# Revit family: 0052419 Sylvania Lighting RANA LED RECESSED
name_source: partatom
category: Lighting Fixtures
revit_build: Autodesk Revit 2016 (Build: 20150220_1215(x64)
units: mm (PartAtom-declared; Revit-internal decimal feet)

## family parameters
Cut with Voids When Loaded = No
Host = Face
Light Source = Yes
OmniClass Number = 23.80.70.00
OmniClass Title = Lighting
Part Type = Normal
Room Calculation Point = No
Round Connector Dimension = Use Diameter
Shared = No

## types (2) — shared parameters
1200_SYL = No
1Ref_SYL = No
2Ref_SYL = No
600x600_SYL = Yes
625x625_SYL = No
Apparent Load = 44 VA
Assembly Code = D5020200
AssetType = Fixed
ClassificationName = Uniclass2015
ClassificationValue = EF_70_80
Color Filter = 16777215
Default Elevation = 1219 mm
Description = Ceiling Recessed LED Linear luminaire (lay-in), with Louvre + Prismatic Optic, Direct Light Distribution, Luminaire Dimensions: 595x595x60mm, Sylvania White body colour, IP20, IK07, Light Engine Dimensions: 570x285mm, Constant Current, Low LED flicker (+/-5%), Emergency 3 hours, Neutral White (4000K) LED Colour Temperature, 4500lm, 44W, 102lm/W efficacy, CRI>80, 3 SDCM (3-step MacAdam ellipse) LED Colour Consistency, UGR<19, Luminance at 65° < 3000 cd/m2, Lumen Maintenance: L90B10 at 50,000 hours, Glow Wire Test 850°C, Quick and easy electrical connection with direct access to push-connectors on top, 2 x metallic safety cables (1.5m) included, the luminaire can be covered with building insulation of Glass Wool type.
Dimming Lamp Color Temperature Shift = <None>
DocumentationLiterature = http://www.sylvania-lighting.com
ElectricShockClassification = Class I
Emit Shape Visible in Rendering = No
Emit from Rectangle Length = 542 mm  [stored 1.77822 ft]
Emit from Rectangle Width = 282 mm
IfcExportAs = IfcLightFixtureType
IfcExportType = IfcLightFixtureType
ImpactProtectionIndex = IK07
IngressProtection = IP20
Inset_SYL = 20 mm  [stored 0.0656168 ft]
Keynote = 16500
Lamp = LED
LampColourRenderingIndex = 80
LampColourTemperature = 4000 K
LampMacAdamStep = 3
LampsType = LED
Length_SYL = 595 mm  [stored 1.9521 ft]
LouverNumber_SYL = 14
Manufacturer = Feilo Sylvania
ManufacturerName = Feilo Sylvania
Material = steel housing, polycarbonate diffuser
Material_1_SYL = Body-Sylvania-Rana-White
Material_2_SYL = <By Category>
Material_3_SYL = <By Category>
Material_4_SYL = <By Category>
Model = RANA LED R 600 HO 4K LOUV+PRI EM W GEN2
ModelNumber = 0052419
ModelReference = RANA LED R 600 HO 4K LOUV+PRI EM W GEN2
Name = RANA LED R 600 HO 4K LOUV+PRI EM W GEN2
NominalDepth = 595 mm  [stored 1.9521 ft]
NominalHeight = 60 mm
NominalLength = 595 mm  [stored 1.9521 ft]
PowerConsumption = 44 W
PowerFactor = 0.95
ReflectorInset_SYL = 30 mm  [stored 0.0984252 ft]
ReflectorLength_SYL = 550 mm
ReflectorNumber_SYL = 3
SlopeBottomWidth_SYL = 593 mm  [stored 1.94554 ft]
SlopeHeight_SYL = 17 mm
SlopeTopWidth_SYL = 410 mm  [stored 1.34514 ft]
Tilt Angle = -90.00°
TopWidth_SYL = 295 mm  [stored 0.967848 ft]
Type Image = <None>
TypeName = RANA LED R 600 HO 4K LOUV+PRI EM W GEN2
URL = http://www.sylvania-lighting.com
Voltage = 0 V
Weight = 4.6 kg
Width_SYL = 595 mm  [stored 1.9521 ft]
zero-valued in all types: Cost

## per-type parameters (varying)
| type | LampNominalLuminous | LuminousEfficacy | Photometric Web File |
| 0052419 RANA LED R 600 HO 4K LOUV+PRI EM | 4500 lm | 102 lm/W | 0052419.ies |
| 0052419 RANA LED R 600 HO 4K LOUV+PRI EM Emergency mode | 560 lm | 12.73 lm/W | 0052419EM.ies |

note: [stored X ft] marks values corroborated as IEEE doubles in the binary element streams (Revit-internal decimal feet)

## geometry (parser evidence)
native form markers: Sweep x9
no freeform markers — native parametric forms only
